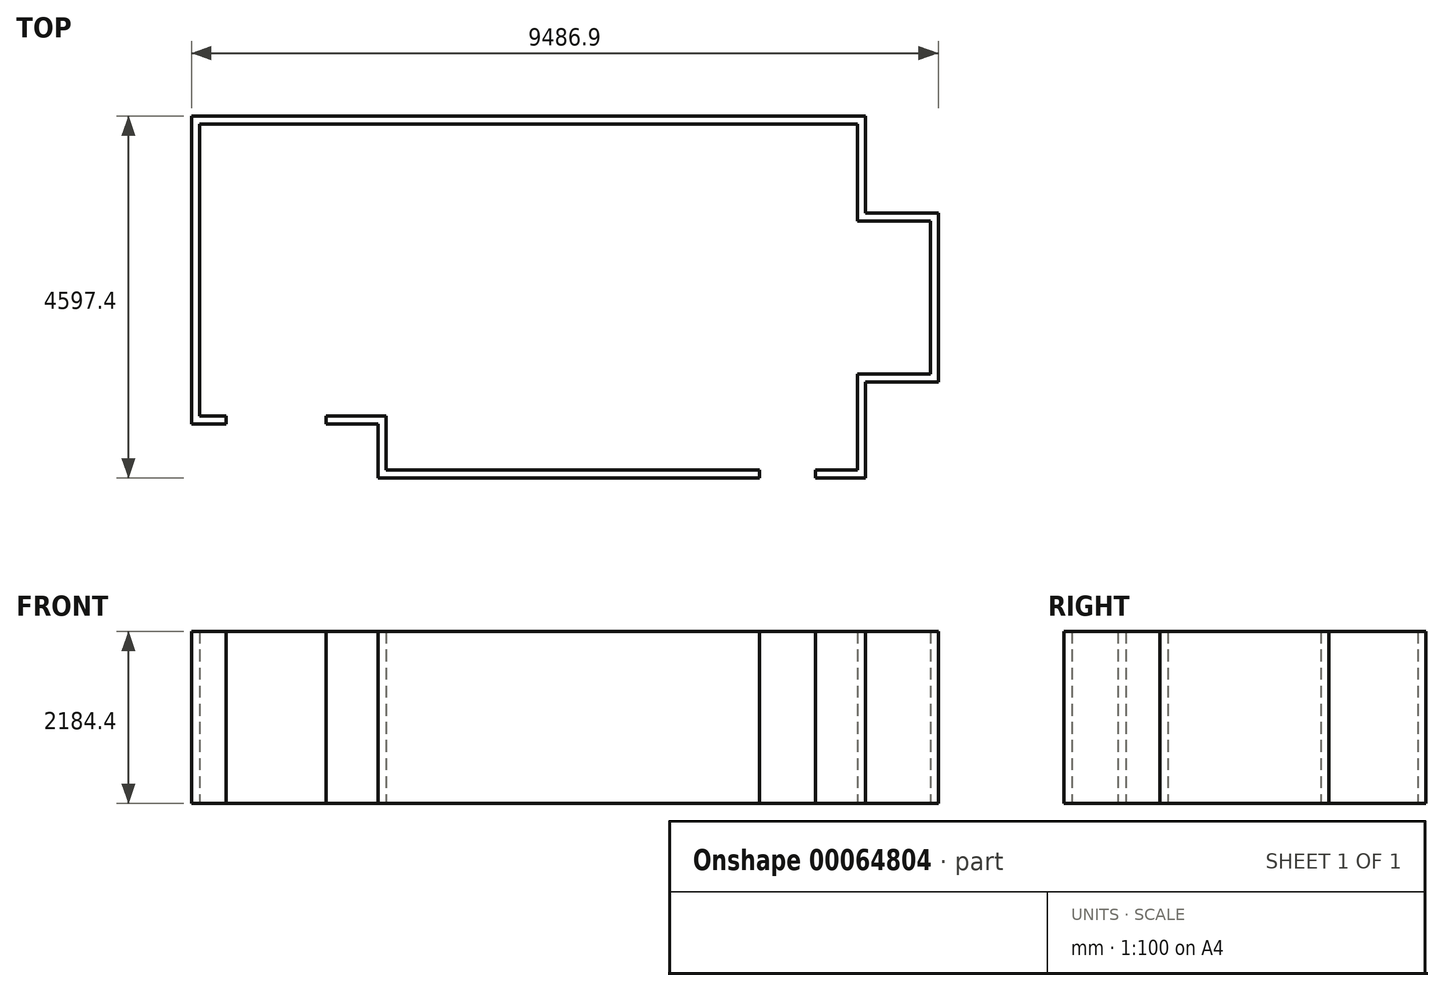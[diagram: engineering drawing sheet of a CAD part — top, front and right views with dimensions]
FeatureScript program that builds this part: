
annotation { "Feature Type Name" : "Feature", "Feature Type Description" : "" }
export const myFeature = defineFeature(function(context is Context, id is Id, definition is map)
    precondition{}
    {
        {
            var Q0;
            Q0=qCreatedBy(makeId("Top.planeOp"),FACE);
            var sketch = newSketch(context, id + "F0", { "sketchPlane" : qUnion([Q0])});
            skLineSegment(sketch, "E0", {"start": v(0, 0) * mm, "end": v(0, -3708.4) * mm});
            skLineSegment(sketch, "E1", {"start": v(0, -3708.4) * mm, "end": v(336.55, -3708.4) * mm});
            skLineSegment(sketch, "E2", {"start": v(1606.55, -3708.4) * mm, "end": v(2368.55, -3708.4) * mm});
            skLineSegment(sketch, "E3", {"start": v(2368.55, -3708.4) * mm, "end": v(2368.55, -4394.2) * mm});
            skLineSegment(sketch, "E4", {"start": v(7823.2, -4394.2) * mm, "end": v(8356.6, -4394.2) * mm});
            skLineSegment(sketch, "E5", {"start": v(8356.6, -4394.2) * mm, "end": v(8356.6, -3175) * mm});
            skLineSegment(sketch, "E6", {"start": v(8356.6, -3175) * mm, "end": v(9283.7, -3175) * mm});
            skLineSegment(sketch, "E7", {"start": v(9283.7, -3175) * mm, "end": v(9283.7, -1231.9) * mm});
            skLineSegment(sketch, "E8", {"start": v(9283.7, -1231.9) * mm, "end": v(8356.6, -1231.9) * mm});
            skLineSegment(sketch, "E9", {"start": v(8356.6, -1231.9) * mm, "end": v(8356.6, 0) * mm});
            skLineSegment(sketch, "E10", {"start": v(0, 0) * mm, "end": v(812.8, 0) * mm});
            skLineSegment(sketch, "E11", {"start": v(812.8, 0) * mm, "end": v(3048, 0) * mm});
            skLineSegment(sketch, "E12", {"start": v(3048, 0) * mm, "end": v(8356.6, 0) * mm});
            skLineSegment(sketch, "E13", {"start": v(7112, -4394.2) * mm, "end": v(2368.55, -4394.2) * mm});
            skLineSegment(sketch, "E14.0", {"start": v(7823.2, -4495.8) * mm, "end": v(8458.2, -4495.8) * mm});
            skLineSegment(sketch, "E14.2", {"start": v(7112, -4495.8) * mm, "end": v(2266.95, -4495.8) * mm});
            skLineSegment(sketch, "E14.3", {"start": v(2266.95, -3810) * mm, "end": v(2266.95, -4495.8) * mm});
            skLineSegment(sketch, "E14.4", {"start": v(1606.55, -3810) * mm, "end": v(2266.95, -3810) * mm});
            skLineSegment(sketch, "E14.5", {"start": v(8458.2, -1130.3) * mm, "end": v(8458.2, 101.6) * mm});
            skLineSegment(sketch, "E14.6", {"start": v(9385.3, -1130.3) * mm, "end": v(8458.2, -1130.3) * mm});
            skLineSegment(sketch, "E14.7", {"start": v(9385.3, -3276.6) * mm, "end": v(9385.3, -1130.3) * mm});
            skLineSegment(sketch, "E14.8", {"start": v(8458.2, -3276.6) * mm, "end": v(9385.3, -3276.6) * mm});
            skLineSegment(sketch, "E14.11", {"start": v(-101.6, 101.6) * mm, "end": v(5651.09, 101.6) * mm});
            skLineSegment(sketch, "E14.12", {"start": v(-101.6, 101.6) * mm, "end": v(-101.6, -3810) * mm});
            skLineSegment(sketch, "E14.13", {"start": v(-101.6, -3810) * mm, "end": v(336.55, -3810) * mm});
            skLineSegment(sketch, "E14.14", {"start": v(8458.2, -4495.8) * mm, "end": v(8458.2, -3276.6) * mm});
            skLineSegment(sketch, "E15", {"start": v(336.55, -3708.4) * mm, "end": v(336.55, -3810) * mm});
            skLineSegment(sketch, "E16", {"start": v(1606.55, -3810) * mm, "end": v(1606.55, -3708.4) * mm});
            skLineSegment(sketch, "E17", {"start": v(7112, -4394.2) * mm, "end": v(7112, -4495.8) * mm});
            skLineSegment(sketch, "E18", {"start": v(7823.2, -4394.2) * mm, "end": v(7823.2, -4495.8) * mm});
            skLineSegment(sketch, "E19", {"start": v(5651.09, 101.6) * mm, "end": v(8458.2, 101.6) * mm});
            skSolve(sketch);
        }
        {
            var Q0;
            Q0=qSketchRegion(id+"F0",true);
            extrude(context, id + "F1", {"entities" : qUnion([Q0]), "depth" : 2184.4 * mm});
        }
    });
